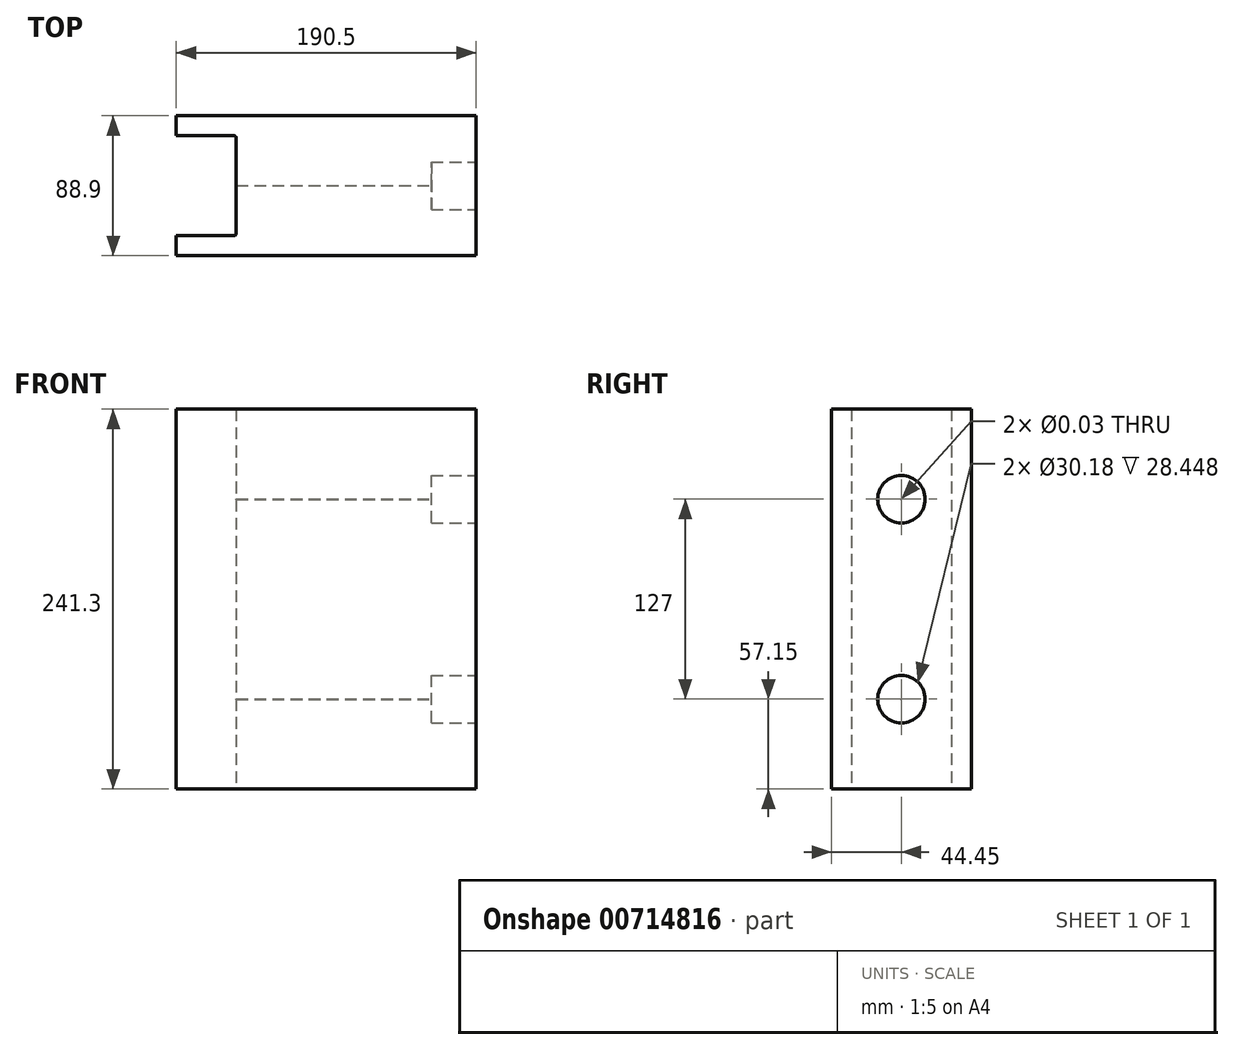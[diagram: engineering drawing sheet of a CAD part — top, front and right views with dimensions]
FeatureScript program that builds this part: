
annotation { "Feature Type Name" : "Feature", "Feature Type Description" : "" }
export const myFeature = defineFeature(function(context is Context, id is Id, definition is map)
    precondition{}
    {
        {
            var Q0;
            Q0=qCreatedBy(makeId("Top.planeOp"),FACE);
            var sketch = newSketch(context, id + "F0", { "sketchPlane" : qUnion([Q0])});
            skLineSegment(sketch, "E0.bottom", {"start": v(-95.25, 44.45) * mm, "end": v(95.25, 44.45) * mm});
            skLineSegment(sketch, "E0.top", {"start": v(-95.25, -44.45) * mm, "end": v(95.25, -44.45) * mm});
            skLineSegment(sketch, "E0.left", {"start": v(-95.25, 44.45) * mm, "end": v(-95.25, 31.75) * mm});
            skLineSegment(sketch, "E0.right", {"start": v(95.25, 44.45) * mm, "end": v(95.25, -44.45) * mm});
            skPoint(sketch, "E0.middle", {"position": v(0, 0) * mm});
            skLineSegment(sketch, "E1.bottom", {"start": v(-133.35, 31.75) * mm, "end": v(-57.15, 31.75) * mm});
            skLineSegment(sketch, "E1.top", {"start": v(-133.35, -31.75) * mm, "end": v(-57.15, -31.75) * mm});
            skLineSegment(sketch, "E1.right", {"start": v(-57.15, 31.75) * mm, "end": v(-57.15, -31.75) * mm});
            skPoint(sketch, "E1.middle", {"position": v(-95.25, 0) * mm});
            skLineSegment(sketch, "E2.trimOffspring", {"start": v(-95.25, -31.75) * mm, "end": v(-95.25, -44.45) * mm});
            skSolve(sketch);
        }
        {
            var Q0;
            Q0 = qSketchRegion(id + "F0", true);
            extrude(context, id + "F1", {"entities" : qUnion([Q0]), "endBound" : BoundingType.SYMMETRIC, "depth" : 241.3 * mm, "offsetDistance" : 25.4 * mm});
        }
        {
            var Q0;
            Q0=makeQuery(id+"F1.opExtrude","SWEPT_FACE",FACE,{"disambiguationData":[OSD([sQuery(id+"F0.wireOp",EDGE,"E0.right")])]});
            var sketch = newSketch(context, id + "F2", { "sketchPlane" : qUnion([Q0])});
            skLineSegment(sketch, "E3.0", {"start": v(44.45, 120.65) * mm, "end": v(-44.45, 120.65) * mm, "construction": true});
            skLineSegment(sketch, "E4", {"start": v(0, 167.27) * mm, "end": v(0, -162.09) * mm, "construction": true});
            skPoint(sketch, "E5.0", {"position": v(-31.75, -120.65) * mm});
            skLineSegment(sketch, "E6.0", {"start": v(44.45, -120.65) * mm, "end": v(-44.45, -120.65) * mm, "construction": true});
            skLineSegment(sketch, "E7.0", {"start": v(44.45, 63.5) * mm, "end": v(-44.45, 63.5) * mm, "construction": true});
            skLineSegment(sketch, "E8.0", {"start": v(44.45, -63.5) * mm, "end": v(-44.45, -63.5) * mm, "construction": true});
            skPoint(sketch, "E9", {"position": v(0, 63.5) * mm});
            skPoint(sketch, "E10", {"position": v(0, -63.5) * mm});
            skSolve(sketch);
        }
        {
            var Q0;
            Q0=sQuery(id+"F2.wireOp",VERTEX,"E9");
            var Q1;
            Q1=sQuery(id+"F2.wireOp",VERTEX,"E10");
            var Q2;
            Q2=makeQuery(id+"F1.opExtrude","SWEPT_BODY",BODY,{"disambiguationData":[OSD([sQuery(id+"F0.wireOp",EDGE,"E0.bottom"),sQuery(id+"F0.wireOp",EDGE,"E0.top"),sQuery(id+"F0.wireOp",EDGE,"E0.left"),sQuery(id+"F0.wireOp",EDGE,"E0.right"),sQuery(id+"F0.wireOp",EDGE,"E1.bottom"),sQuery(id+"F0.wireOp",EDGE,"E1.top"),sQuery(id+"F0.wireOp",EDGE,"E1.right"),sQuery(id+"F0.wireOp",EDGE,"E2.trimOffspring")])]});
            hole(context, id + "F3", {"style" : HoleStyle.C_BORE, "endStyle" : HoleEndStyle.THROUGH, "standardTappedOrClearance" : lookupTablePath({ "standard" : "ANSI", "size" : "13/16 (0.81)", "type" : "Drilled" }), "standardBlindInLast" : lookupTablePath({ "standard" : "ANSI", "size" : "13/16", "type" : "Drilled" }), "holeDiameter" : 13 / 406.4 * mm, "cBoreDiameter" : 30.18 * mm, "cBoreDepth" : 28.45 * mm, "majorDiameter" : 6.35 * mm, "isTappedThrough" : true, "tappedDepth" : 34.3 * mm, "tapClearance" : 3, "locations" : qUnion([Q0, Q1]), "scope" : qUnion([Q2])});
        }
        {
            var Q0;
            Q0=makeQuery(id+"F1.opExtrude","SWEPT_EDGE",EDGE,{"disambiguationData":[OSD([sQuery(id+"F0.wireOp",EDGE,"E1.top"),sQuery(id+"F0.wireOp",EDGE,"E1.right")])]});
            var Q1;
            Q1=makeQuery(id+"F1.opExtrude","SWEPT_EDGE",EDGE,{"disambiguationData":[OSD([sQuery(id+"F0.wireOp",EDGE,"E1.bottom"),sQuery(id+"F0.wireOp",EDGE,"E1.right")])]});
            fillet(context, id + "F4", {"entities" : qUnion([Q0, Q1]), "radius" : 1.52 * mm, "tangentPropagation" : true, "allowEdgeOverflow" : false});
        }
    });
